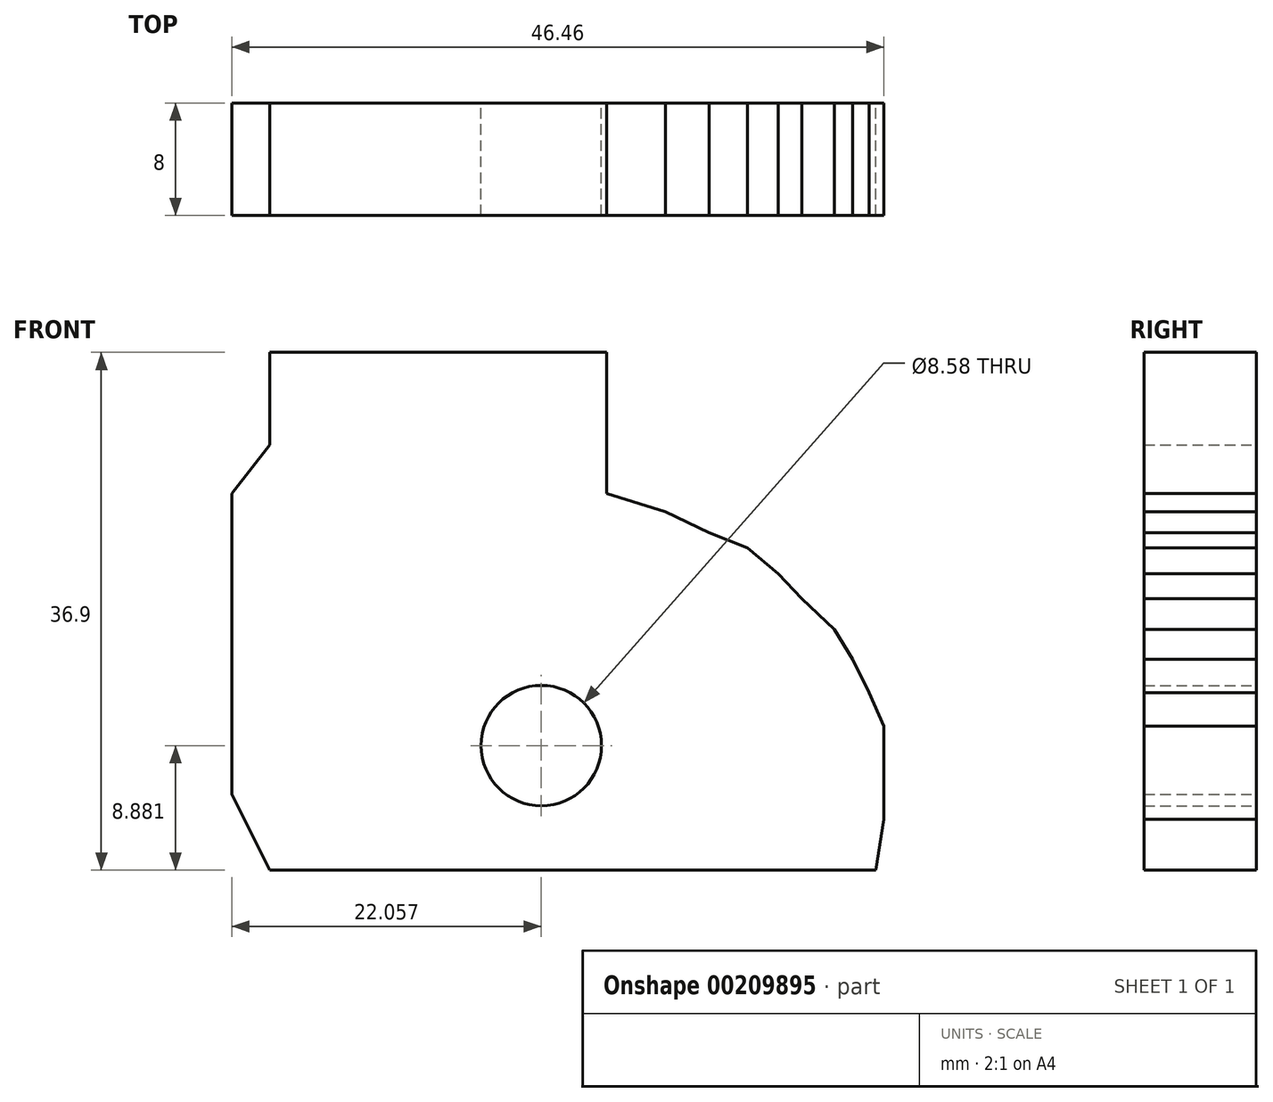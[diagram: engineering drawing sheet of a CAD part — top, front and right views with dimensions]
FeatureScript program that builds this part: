
annotation { "Feature Type Name" : "Feature", "Feature Type Description" : "" }
export const myFeature = defineFeature(function(context is Context, id is Id, definition is map)
    precondition{}
    {
        {
            var Q0;
            Q0=qCreatedBy(makeId("Front.planeOp"),FACE);
            var sketch = newSketch(context, id + "F0", { "sketchPlane" : qUnion([Q0])});
            skLineSegment(sketch, "E0", {"start": v(-24, -26.85) * mm, "end": v(19.2, -26.85) * mm});
            skLineSegment(sketch, "E1", {"start": v(-24, -26.85) * mm, "end": v(-26.7, -21.45) * mm});
            skLineSegment(sketch, "E2", {"start": v(-26.7, -21.45) * mm, "end": v(-26.7, 0) * mm});
            skLineSegment(sketch, "E3", {"start": v(-26.7, 0) * mm, "end": v(-24, 3.45) * mm});
            skLineSegment(sketch, "E4", {"start": v(-24, 3.45) * mm, "end": v(-24, 10.05) * mm});
            skLineSegment(sketch, "E5", {"start": v(-24, 10.05) * mm, "end": v(0, 10.05) * mm});
            skLineSegment(sketch, "E6", {"start": v(0, 10.05) * mm, "end": v(0, 0) * mm});
            skPoint(sketch, "E7", {"position": v(4.2, -1.3) * mm});
            skPoint(sketch, "E8", {"position": v(7.3, -2.8) * mm});
            skPoint(sketch, "E9", {"position": v(10.04, -3.87) * mm});
            skPoint(sketch, "E10", {"position": v(12.25, -5.72) * mm});
            skPoint(sketch, "E11", {"position": v(13.93, -7.5) * mm});
            skPoint(sketch, "E12", {"position": v(16.23, -9.7) * mm});
            skPoint(sketch, "E13", {"position": v(17.55, -11.82) * mm});
            skPoint(sketch, "E14", {"position": v(18.7, -14.21) * mm});
            skPoint(sketch, "E15", {"position": v(18.7, -16.6) * mm});
            skPoint(sketch, "E16", {"position": v(19.76, -19.87) * mm});
            skPoint(sketch, "E17", {"position": v(19.76, -22.43) * mm});
            skPoint(sketch, "E18", {"position": v(19.76, -25.7) * mm});
            skPoint(sketch, "E19", {"position": v(19.2, -26.85) * mm});
            skPoint(sketch, "E20", {"position": v(19.76, -16.6) * mm});
            skLineSegment(sketch, "E21", {"start": v(0, 0) * mm, "end": v(4.2, -1.3) * mm});
            skLineSegment(sketch, "E22", {"start": v(4.2, -1.3) * mm, "end": v(7.3, -2.8) * mm});
            skLineSegment(sketch, "E23", {"start": v(7.3, -2.8) * mm, "end": v(10.04, -3.87) * mm});
            skLineSegment(sketch, "E24", {"start": v(10.04, -3.87) * mm, "end": v(12.25, -5.72) * mm});
            skLineSegment(sketch, "E25", {"start": v(12.25, -5.72) * mm, "end": v(13.93, -7.5) * mm});
            skLineSegment(sketch, "E26", {"start": v(13.93, -7.5) * mm, "end": v(16.23, -9.7) * mm});
            skLineSegment(sketch, "E27", {"start": v(16.23, -9.7) * mm, "end": v(17.55, -11.82) * mm});
            skLineSegment(sketch, "E28", {"start": v(17.55, -11.82) * mm, "end": v(18.7, -14.21) * mm});
            skLineSegment(sketch, "E29", {"start": v(18.7, -14.21) * mm, "end": v(19.76, -16.6) * mm});
            skLineSegment(sketch, "E30", {"start": v(19.76, -16.6) * mm, "end": v(19.76, -19.87) * mm});
            skLineSegment(sketch, "E31", {"start": v(19.76, -19.87) * mm, "end": v(19.76, -23.23) * mm});
            skLineSegment(sketch, "E32", {"start": v(19.76, -23.23) * mm, "end": v(19.2, -26.85) * mm});
            skCircle(sketch, "E33", {"center": v(-4.64, -17.97) * mm, "radius": 4.29 * mm});
            skSolve(sketch);
        }
        {
            var Q0;
            Q0=makeQuery(id+"F0.imprint","IMPRINT",FACE,{"disambiguationData":[TD([[makeQuery(id+"F0.imprint","IMPRINT",EDGE,{"derivedFrom":sQuery(id+"F0.wireOp",EDGE,"E0")}),1.0]])]});
            extrude(context, id + "F1", {"entities" : qUnion([Q0]), "depth" : 8 * mm});
        }
    });
